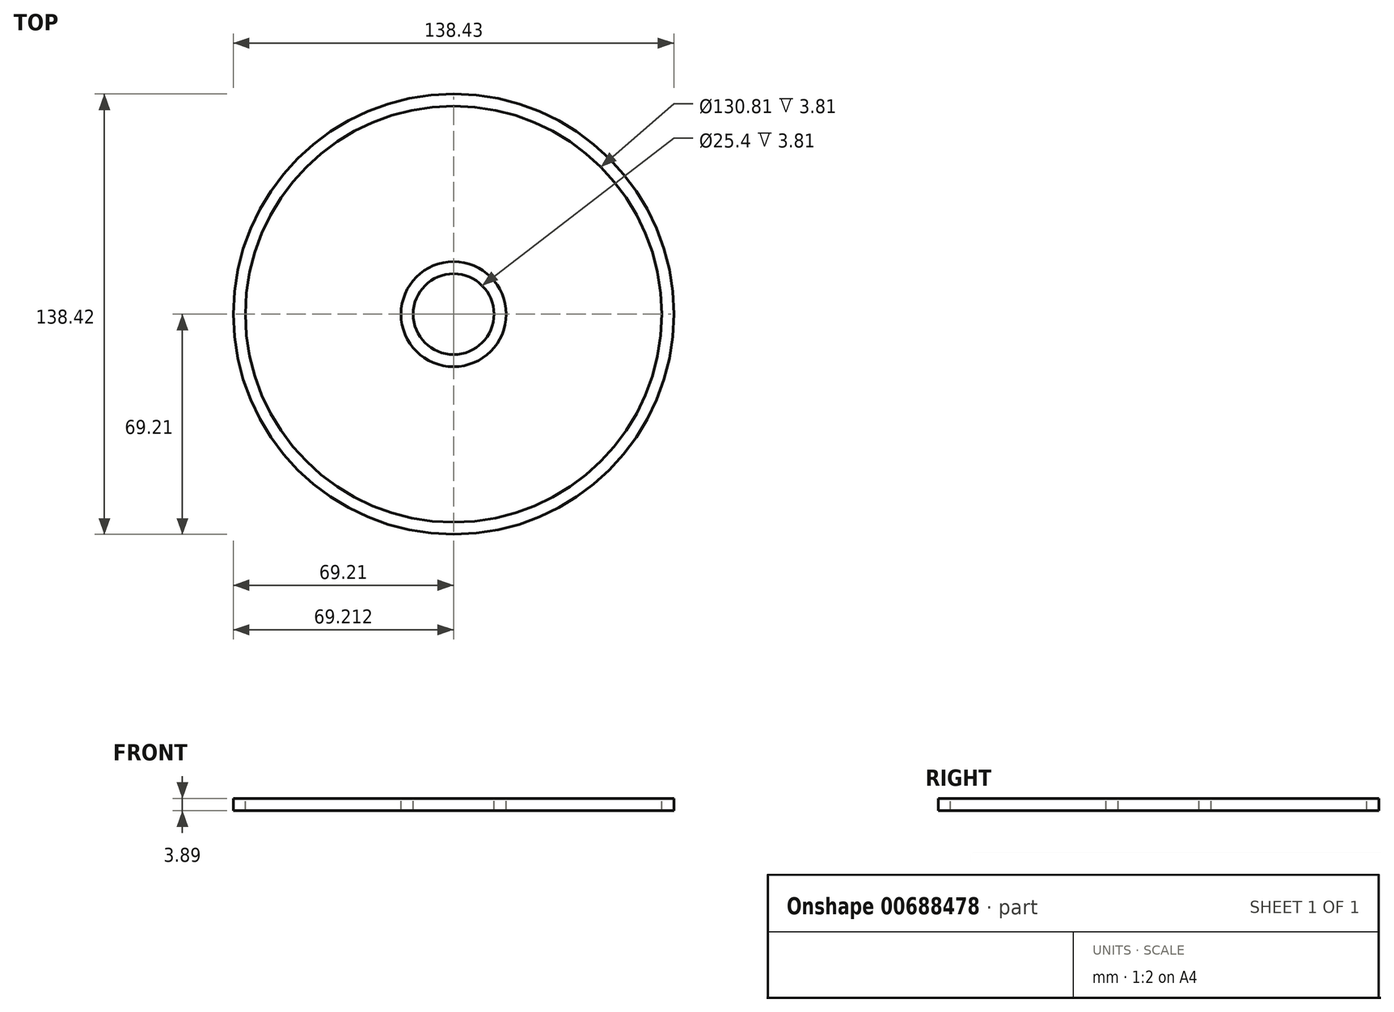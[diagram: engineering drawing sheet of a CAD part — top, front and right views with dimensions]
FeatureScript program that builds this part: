
annotation { "Feature Type Name" : "Feature", "Feature Type Description" : "" }
export const myFeature = defineFeature(function(context is Context, id is Id, definition is map)
    precondition{}
    {
        {
            var Q0;
            Q0=qCreatedBy(makeId("Front.planeOp"),FACE);
            var sketch = newSketch(context, id + "F0", { "sketchPlane" : qUnion([Q0])});
            skLineSegment(sketch, "E0.bottom", {"start": v(16.51, 1.9) * mm, "end": v(12.7, 1.9) * mm});
            skLineSegment(sketch, "E0.top", {"start": v(16.51, -1.9) * mm, "end": v(12.7, -1.9) * mm});
            skLineSegment(sketch, "E0.left", {"start": v(16.51, 1.9) * mm, "end": v(16.51, -1.9) * mm});
            skLineSegment(sketch, "E0.right", {"start": v(12.7, 1.9) * mm, "end": v(12.7, -1.9) * mm});
            skPoint(sketch, "E0.middle", {"position": v(14.6, 0) * mm});
            skLineSegment(sketch, "E1", {"start": v(0, 3.85) * mm, "end": v(0, -3) * mm});
            skSolve(sketch);
        }
        {
            var Q0;
            Q0=makeQuery(id+"F0.imprint","IMPRINT",FACE,{"disambiguationData":[TD([[makeQuery(id+"F0.imprint","IMPRINT",EDGE,{"derivedFrom":sQuery(id+"F0.wireOp",EDGE,"E0.bottom")}),1.0]])]});
            var Q1;
            Q1=sQuery(id+"F0.wireOp",EDGE,"E1");
            revolve(context, id + "F1", {"entities" : qUnion([Q0]), "axis" : qUnion([Q1]), "revolveType" : RevolveType.FULL});
        }
        {
            var Q0;
            Q0=qCreatedBy(makeId("Front.planeOp"),FACE);
            var sketch = newSketch(context, id + "F2", { "sketchPlane" : qUnion([Q0])});
            skLineSegment(sketch, "E2.bottom", {"start": v(69.22, 1.83) * mm, "end": v(65.4, 1.83) * mm});
            skLineSegment(sketch, "E2.top", {"start": v(69.22, -1.98) * mm, "end": v(65.4, -1.98) * mm});
            skLineSegment(sketch, "E2.left", {"start": v(69.22, 1.83) * mm, "end": v(69.22, -1.98) * mm});
            skLineSegment(sketch, "E2.right", {"start": v(65.4, 1.83) * mm, "end": v(65.4, -1.98) * mm});
            skPoint(sketch, "E2.middle", {"position": v(67.31, -0.07) * mm});
            skLineSegment(sketch, "E3", {"start": v(0, 3.78) * mm, "end": v(0, -3.07) * mm});
            skSolve(sketch);
        }
        {
            var Q0;
            Q0=makeQuery(id+"F2.imprint","IMPRINT",FACE,{"disambiguationData":[TD([[makeQuery(id+"F2.imprint","IMPRINT",EDGE,{"derivedFrom":sQuery(id+"F2.wireOp",EDGE,"E2.bottom")}),1.0]])]});
            var Q1;
            Q1=sQuery(id+"F2.wireOp",EDGE,"E3");
            revolve(context, id + "F3", {"entities" : qUnion([Q0]), "axis" : qUnion([Q1]), "revolveType" : RevolveType.FULL});
        }
    });
